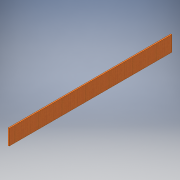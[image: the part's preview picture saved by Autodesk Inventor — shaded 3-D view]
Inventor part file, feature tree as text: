
AUTODESK INVENTOR PART (.ipt)
format: ipt  version: 2016 (Build 200138000, 138)  size: 94,720 bytes
history: native  units: in
note: dims shown in document units (in); Inventor stores cm internally (conversion verified against a paired STEP export)
features: extrude x1, sketch x1
ambient origin geometry x8: Origin, YZ Plane, XZ Plane, XY Plane, X Axis, Y Axis, Z Axis, Center Point
bodies: Solid1 (feature_tree)
feature tree (2):
  extrude  "Extrusion1"  Depth=6.5in
  sketch  "Sketch1"  dims[d0=69.0in d1=6.5in d2=0.4375in d3=0.0in]
